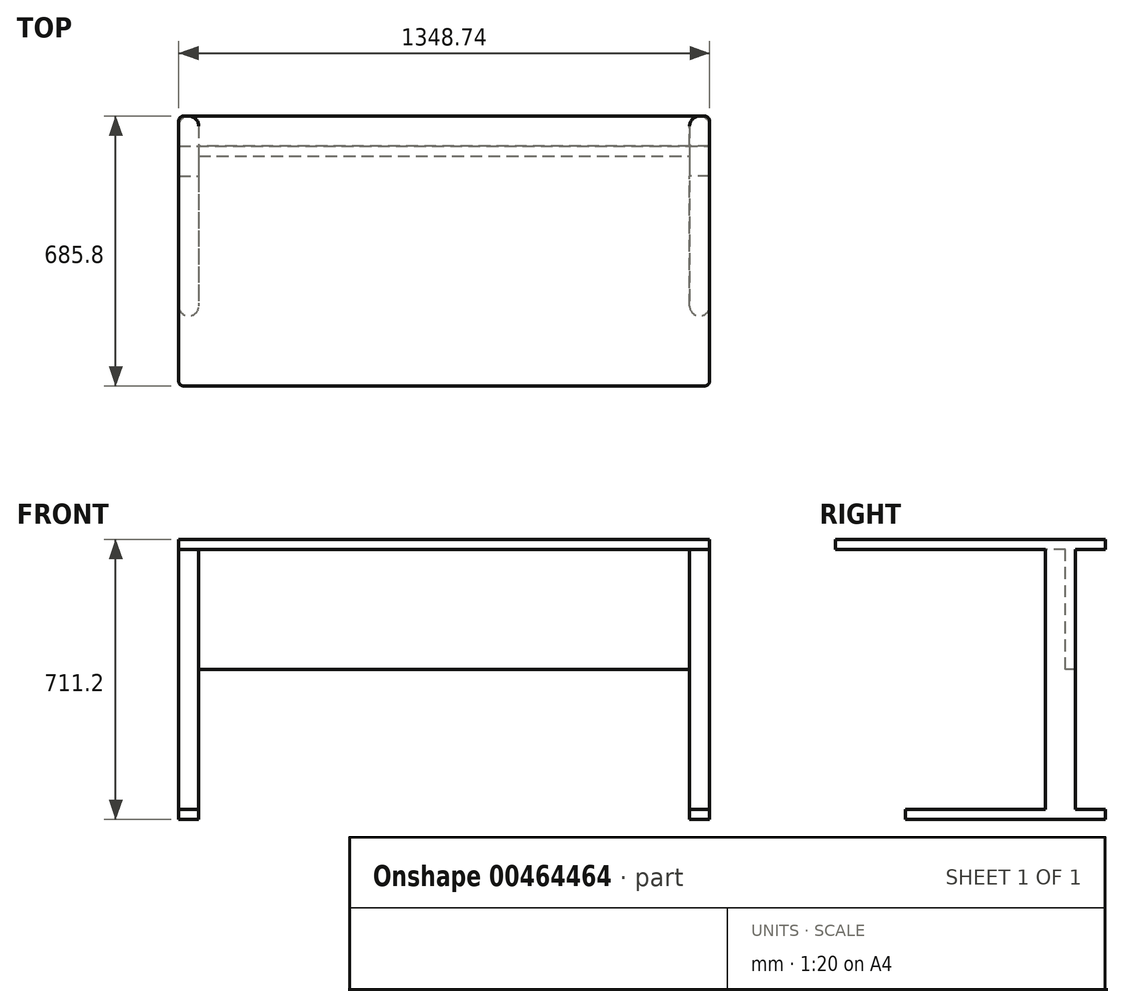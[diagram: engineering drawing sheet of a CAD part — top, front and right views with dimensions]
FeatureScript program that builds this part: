
annotation { "Feature Type Name" : "Feature", "Feature Type Description" : "" }
export const myFeature = defineFeature(function(context is Context, id is Id, definition is map)
    precondition{}
    {
        {
            var Q0;
            Q0=qCreatedBy(makeId("Top.planeOp"),FACE);
            var sketch = newSketch(context, id + "F0", { "sketchPlane" : qUnion([Q0])});
            skPoint(sketch, "E0.middle", {"position": v(-550.28, 186.25) * mm});
            skLineSegment(sketch, "E1.bottom", {"start": v(674.37, 342.9) * mm, "end": v(-674.37, 342.9) * mm});
            skLineSegment(sketch, "E1.top", {"start": v(674.37, -342.9) * mm, "end": v(-674.37, -342.9) * mm});
            skLineSegment(sketch, "E1.left", {"start": v(674.37, 342.9) * mm, "end": v(674.37, -342.9) * mm});
            skLineSegment(sketch, "E1.right", {"start": v(-674.37, 342.9) * mm, "end": v(-674.37, -342.9) * mm});
            skPoint(sketch, "E1.middle", {"position": v(0, 0) * mm});
            skSolve(sketch);
        }
        {
            var Q0;
            Q0=makeQuery(id+"F0.imprint","IMPRINT",FACE,{"disambiguationData":[TD([[makeQuery(id+"F0.imprint","IMPRINT",EDGE,{"derivedFrom":sQuery(id+"F0.wireOp",EDGE,"E1.bottom")}),1.0]])]});
            extrude(context, id + "F1", {"entities" : qUnion([Q0]), "depth" : 25.4 * mm});
        }
        {
            var Q0;
            Q0=makeQuery(id+"F1.opExtrude","CAP_FACE",FACE,{"disambiguationData":[OSD([sQuery(id+"F0.wireOp",EDGE,"E1.bottom"),sQuery(id+"F0.wireOp",EDGE,"E1.top"),sQuery(id+"F0.wireOp",EDGE,"E1.left"),sQuery(id+"F0.wireOp",EDGE,"E1.right")])],"isStart":false});
            var sketch = newSketch(context, id + "F2", { "sketchPlane" : qUnion([Q0])});
            skLineSegment(sketch, "E2.bottom", {"start": v(-674.37, 266.7) * mm, "end": v(-623.57, 266.7) * mm});
            skLineSegment(sketch, "E2.top", {"start": v(-674.37, 190.5) * mm, "end": v(-623.57, 190.5) * mm});
            skLineSegment(sketch, "E2.left", {"start": v(-674.37, 266.7) * mm, "end": v(-674.37, 190.5) * mm});
            skLineSegment(sketch, "E2.right", {"start": v(-623.57, 266.7) * mm, "end": v(-623.57, 190.5) * mm});
            skLineSegment(sketch, "E3.bottom", {"start": v(674.37, 266.7) * mm, "end": v(623.57, 266.7) * mm});
            skLineSegment(sketch, "E3.top", {"start": v(674.37, 190.5) * mm, "end": v(623.57, 190.5) * mm});
            skLineSegment(sketch, "E3.left", {"start": v(674.37, 266.7) * mm, "end": v(674.37, 190.5) * mm});
            skLineSegment(sketch, "E3.right", {"start": v(623.57, 266.7) * mm, "end": v(623.57, 190.5) * mm});
            skSolve(sketch);
        }
        {
            var Q0;
            Q0=makeQuery(id+"F2.imprint","IMPRINT",FACE,{"disambiguationData":[TD([[makeQuery(id+"F2.imprint","IMPRINT",EDGE,{"derivedFrom":sQuery(id+"F2.wireOp",EDGE,"E2.bottom")}),-1.0]])]});
            var Q1;
            Q1=makeQuery(id+"F2.imprint","IMPRINT",FACE,{"disambiguationData":[TD([[makeQuery(id+"F2.imprint","IMPRINT",EDGE,{"derivedFrom":sQuery(id+"F2.wireOp",EDGE,"E3.bottom")}),1.0]])]});
            extrude(context, id + "F3", {"entities" : qUnion([Q0, Q1]), "operationType" : NewBodyOperationType.ADD, "oppositeDirection" : true, "depth" : 711.2 * mm});
        }
        {
            var Q0;
            Q0=makeQuery(id+"F3.boolean.opBoolean","MERGE",FACE,{"derivedFrom":[makeQuery(id+"F1.opExtrude","SWEPT_FACE",FACE,{"disambiguationData":[OSD([sQuery(id+"F0.wireOp",EDGE,"E1.right")])]}),makeQuery(id+"F3.opExtrude","SWEPT_FACE",FACE,{"disambiguationData":[OSD([sQuery(id+"F2.wireOp",EDGE,"E2.left")])]})]});
            var sketch = newSketch(context, id + "F4", { "sketchPlane" : qUnion([Q0])});
            skPoint(sketch, "E4.oppositeSnap0", {"position": v(-228.6, -685.8) * mm});
            skLineSegment(sketch, "E4.bottom", {"start": v(-342.9, -660.4) * mm, "end": v(165.1, -660.4) * mm});
            skLineSegment(sketch, "E4.top", {"start": v(-342.9, -685.8) * mm, "end": v(165.1, -685.8) * mm});
            skLineSegment(sketch, "E4.left", {"start": v(-342.9, -660.4) * mm, "end": v(-342.9, -685.8) * mm});
            skLineSegment(sketch, "E4.right", {"start": v(165.1, -660.4) * mm, "end": v(165.1, -685.8) * mm});
            skSolve(sketch);
        }
        {
            var Q0;
            Q0 = qSketchRegion(id + "F4", true);
            var Q1;
            {var subQ0=sQuery(id+"F4.wireOp",EDGE,"E4.left");Q1=makeQuery(id+"F4.imprint","IMPRINT",FACE,{"disambiguationData":[TD([[makeQuery(id+"F4.imprint","IMPRINT",EDGE,{"derivedFrom":subQ0}),1.0]])]});}
            extrude(context, id + "F5", {"entities" : qUnion([Q0, Q1]), "operationType" : NewBodyOperationType.ADD, "oppositeDirection" : true, "depth" : 50.8 * mm});
        }
        {
            var Q0;
            Q0=makeQuery(id+"F3.boolean.opBoolean","MERGE",FACE,{"derivedFrom":[makeQuery(id+"F1.opExtrude","SWEPT_FACE",FACE,{"disambiguationData":[OSD([sQuery(id+"F0.wireOp",EDGE,"E1.left")])]}),makeQuery(id+"F3.opExtrude","SWEPT_FACE",FACE,{"disambiguationData":[OSD([sQuery(id+"F2.wireOp",EDGE,"E3.left")])]})]});
            var sketch = newSketch(context, id + "F6", { "sketchPlane" : qUnion([Q0])});
            skLineSegment(sketch, "E5.bottom", {"start": v(-165.1, -660.4) * mm, "end": v(342.9, -660.4) * mm});
            skLineSegment(sketch, "E5.top", {"start": v(-165.1, -685.8) * mm, "end": v(342.9, -685.8) * mm});
            skLineSegment(sketch, "E5.left", {"start": v(-165.1, -660.4) * mm, "end": v(-165.1, -685.8) * mm});
            skLineSegment(sketch, "E5.right", {"start": v(342.9, -660.4) * mm, "end": v(342.9, -685.8) * mm});
            skSolve(sketch);
        }
        {
            var Q0;
            {var subQ0=sQuery(id+"F6.wireOp",EDGE,"E5.left");Q0=makeQuery(id+"F6.imprint","IMPRINT",FACE,{"disambiguationData":[TD([[makeQuery(id+"F6.imprint","IMPRINT",EDGE,{"derivedFrom":subQ0}),1.0]])]});}
            var Q1;
            {var subQ0=sQuery(id+"F6.wireOp",EDGE,"E5.bottom");var subQ1=sQuery(id+"F2.wireOp",EDGE,"E3.left");var subQ2=sQuery(id+"F0.wireOp",EDGE,"E1.left");var subQ3=makeQuery(id+"F3.opExtrude","SWEPT_EDGE",EDGE,{"disambiguationData":[OSD([subQ2,sQuery(id+"F2.wireOp",EDGE,"E3.top"),subQ1])]});var subQ4=makeQuery(id+"F6.imprint","INTERSECT",VERTEX,{"derivedFrom":[subQ3,subQ0]});Q1=makeQuery(id+"F6.imprint","IMPRINT",FACE,{"disambiguationData":[TD([[makeQuery(id+"F6.imprint","IMPRINT",EDGE,{"disambiguationData":[TD([[subQ4,-1.0]])],"derivedFrom":subQ0}),-1.0]])]});}
            var Q2;
            {var subQ0=sQuery(id+"F6.wireOp",EDGE,"E5.right");Q2=makeQuery(id+"F6.imprint","IMPRINT",FACE,{"disambiguationData":[TD([[makeQuery(id+"F6.imprint","IMPRINT",EDGE,{"derivedFrom":subQ0}),-1.0]])]});}
            extrude(context, id + "F7", {"entities" : qUnion([Q0, Q1, Q2]), "operationType" : NewBodyOperationType.ADD, "oppositeDirection" : true, "depth" : 50.8 * mm});
        }
        {
            var Q0;
            Q0=makeQuery(id+"F1.opExtrude","CAP_FACE",FACE,{"disambiguationData":[OSD([sQuery(id+"F0.wireOp",EDGE,"E1.bottom"),sQuery(id+"F0.wireOp",EDGE,"E1.top"),sQuery(id+"F0.wireOp",EDGE,"E1.left"),sQuery(id+"F0.wireOp",EDGE,"E1.right")])],"isStart":true});
            var sketch = newSketch(context, id + "F8", { "sketchPlane" : qUnion([Q0])});
            skLineSegment(sketch, "E6.bottom", {"start": v(-674.37, -266.7) * mm, "end": v(674.37, -266.7) * mm});
            skLineSegment(sketch, "E6.top", {"start": v(-674.37, -241.3) * mm, "end": v(674.37, -241.3) * mm});
            skLineSegment(sketch, "E6.left", {"start": v(-674.37, -266.7) * mm, "end": v(-674.37, -241.3) * mm});
            skLineSegment(sketch, "E6.right", {"start": v(674.37, -266.7) * mm, "end": v(674.37, -241.3) * mm});
            skSolve(sketch);
        }
        {
            var Q0;
            Q0 = qSketchRegion(id + "F8", true);
            extrude(context, id + "F9", {"entities" : qUnion([Q0]), "operationType" : NewBodyOperationType.ADD, "depth" : 304.8 * mm});
        }
        {
            var Q0;
            Q0=makeQuery(id+"F1.opExtrude","SWEPT_EDGE",EDGE,{"disambiguationData":[OSD([sQuery(id+"F0.wireOp",EDGE,"E1.top"),sQuery(id+"F0.wireOp",EDGE,"E1.left")])]});
            var Q1;
            Q1=makeQuery(id+"F1.opExtrude","SWEPT_EDGE",EDGE,{"disambiguationData":[OSD([sQuery(id+"F0.wireOp",EDGE,"E1.top"),sQuery(id+"F0.wireOp",EDGE,"E1.right")])]});
            var Q2;
            Q2=makeQuery(id+"F1.opExtrude","SWEPT_EDGE",EDGE,{"disambiguationData":[OSD([sQuery(id+"F0.wireOp",EDGE,"E1.bottom"),sQuery(id+"F0.wireOp",EDGE,"E1.right")])]});
            var Q3;
            Q3=makeQuery(id+"F1.opExtrude","SWEPT_EDGE",EDGE,{"disambiguationData":[OSD([sQuery(id+"F0.wireOp",EDGE,"E1.bottom"),sQuery(id+"F0.wireOp",EDGE,"E1.left")])]});
            fillet(context, id + "F10", {"entities" : qUnion([Q0, Q1, Q2, Q3]), "radius" : 12.7 * mm, "tangentPropagation" : true, "allowEdgeOverflow" : false});
        }
        {
            var Q0;
            Q0=makeQuery(id+"F5.opExtrude","CAP_EDGE",EDGE,{"disambiguationData":[OSD([sQuery(id+"F4.wireOp",EDGE,"E4.right")])],"isStart":false});
            var Q1;
            Q1=makeQuery(id+"F5.opExtrude","CAP_EDGE",EDGE,{"disambiguationData":[OSD([sQuery(id+"F4.wireOp",EDGE,"E4.right")])],"isStart":true});
            var Q2;
            Q2=makeQuery(id+"F7.opExtrude","CAP_EDGE",EDGE,{"disambiguationData":[OSD([sQuery(id+"F6.wireOp",EDGE,"E5.left")])],"isStart":true});
            var Q3;
            Q3=makeQuery(id+"F7.opExtrude","CAP_EDGE",EDGE,{"disambiguationData":[OSD([sQuery(id+"F6.wireOp",EDGE,"E5.left")])],"isStart":false});
            var Q4;
            Q4=makeQuery(id+"F7.opExtrude","CAP_EDGE",EDGE,{"disambiguationData":[OSD([sQuery(id+"F6.wireOp",EDGE,"E5.right")])],"isStart":true});
            var Q5;
            Q5=makeQuery(id+"F7.opExtrude","CAP_EDGE",EDGE,{"disambiguationData":[OSD([sQuery(id+"F6.wireOp",EDGE,"E5.right")])],"isStart":false});
            var Q6;
            Q6=makeQuery(id+"F5.opExtrude","CAP_EDGE",EDGE,{"disambiguationData":[OSD([sQuery(id+"F4.wireOp",EDGE,"E4.left")])],"isStart":true});
            var Q7;
            Q7=makeQuery(id+"F5.opExtrude","CAP_EDGE",EDGE,{"disambiguationData":[OSD([sQuery(id+"F4.wireOp",EDGE,"E4.left")])],"isStart":false});
            fillet(context, id + "F11", {"entities" : qUnion([Q0, Q1, Q2, Q3, Q4, Q5, Q6, Q7]), "radius" : 25.4 * mm, "tangentPropagation" : true, "allowEdgeOverflow" : false});
        }
    });
